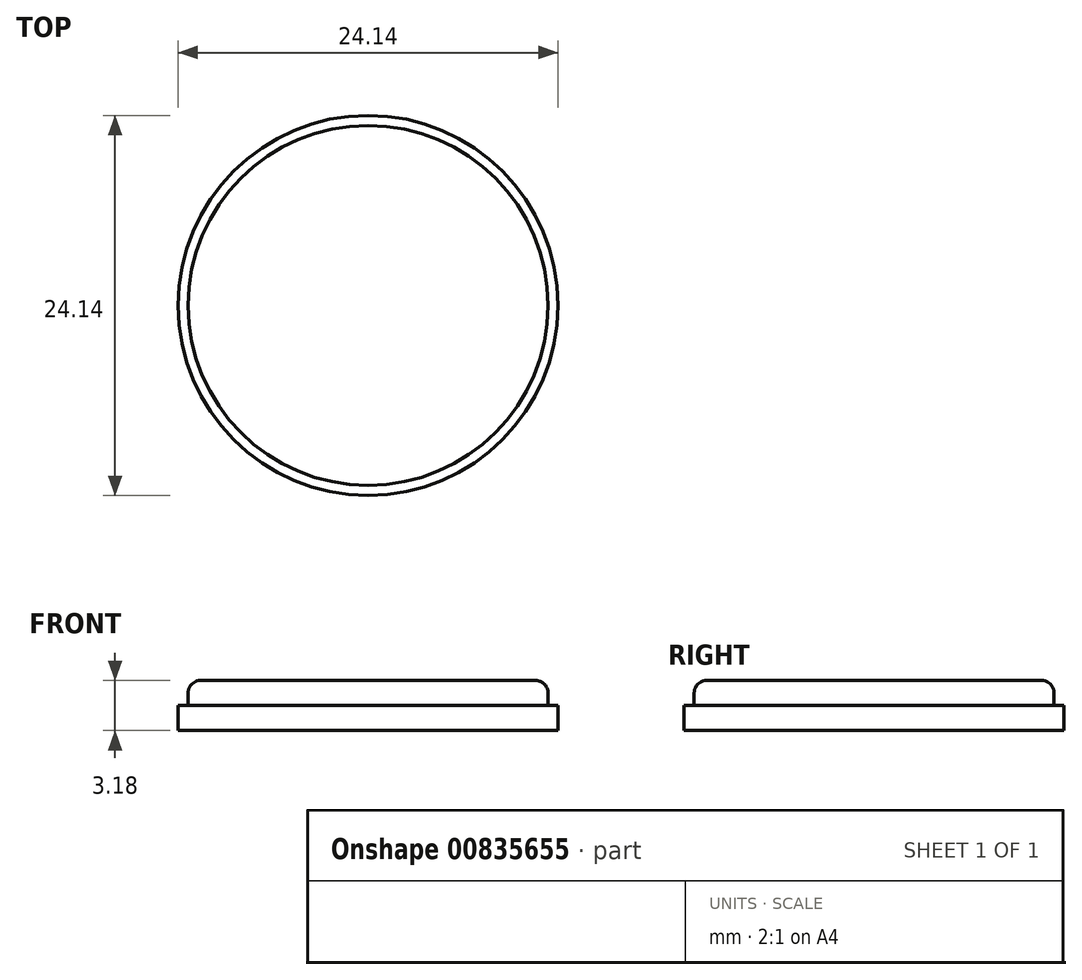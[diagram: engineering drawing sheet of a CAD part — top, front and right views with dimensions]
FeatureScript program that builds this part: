
annotation { "Feature Type Name" : "Feature", "Feature Type Description" : "" }
export const myFeature = defineFeature(function(context is Context, id is Id, definition is map)
    precondition{}
    {
        {
            var Q0;
            Q0=qCreatedBy(makeId("Top.planeOp"),FACE);
            var sketch = newSketch(context, id + "F0", { "sketchPlane" : qUnion([Q0])});
            skCircle(sketch, "E0", {"center": v(0, 0) * mm, "radius": 12.07 * mm});
            skSolve(sketch);
        }
        {
            var Q0;
            Q0=qSketchRegion(id+"F0",true);
            extrude(context, id + "F1", {"entities" : qUnion([Q0]), "depth" : 1.59 * mm, "offsetDistance" : 25.4 * mm});
        }
        {
            var Q0;
            Q0=makeQuery(id+"F1.opExtrude","CAP_FACE",FACE,{"disambiguationData":[OSD([sQuery(id+"F0.wireOp",EDGE,"E0")])],"isStart":false});
            var sketch = newSketch(context, id + "F2", { "sketchPlane" : qUnion([Q0])});
            skCircle(sketch, "E1", {"center": v(0, 0) * mm, "radius": 11.43 * mm});
            skSolve(sketch);
        }
        {
            var Q0;
            Q0=makeQuery(id+"F2.imprint","IMPRINT",FACE,{"disambiguationData":[TD([[makeQuery(id+"F2.imprint","IMPRINT",EDGE,{"derivedFrom":sQuery(id+"F2.wireOp",EDGE,"E1")}),1.0]])]});
            extrude(context, id + "F3", {"entities" : qUnion([Q0]), "operationType" : NewBodyOperationType.ADD, "depth" : 1.59 * mm, "offsetDistance" : 25.4 * mm});
        }
        {
            var Q0;
            Q0=makeQuery(id+"F3.opExtrude","CAP_EDGE",EDGE,{"disambiguationData":[OSD([sQuery(id+"F2.wireOp",EDGE,"E1")])],"isStart":false});
            fillet(context, id + "F4", {"entities" : qUnion([Q0]), "radius" : 0.8 * mm, "tangentPropagation" : true, "allowEdgeOverflow" : false});
        }
    });
